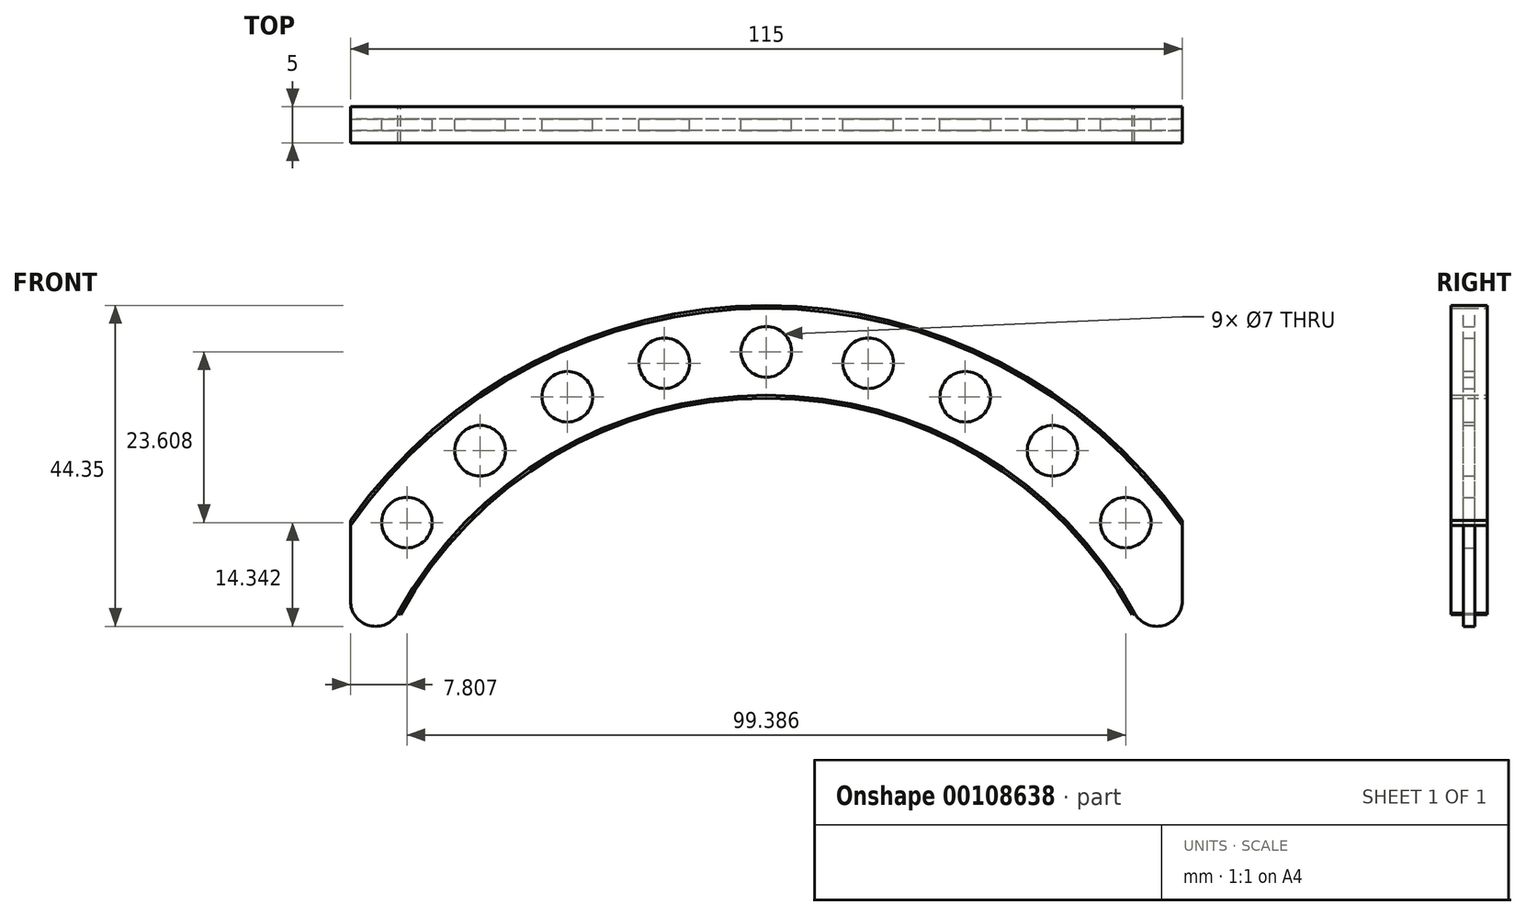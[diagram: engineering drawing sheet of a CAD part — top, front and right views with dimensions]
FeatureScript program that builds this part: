
annotation { "Feature Type Name" : "Feature", "Feature Type Description" : "" }
export const myFeature = defineFeature(function(context is Context, id is Id, definition is map)
    precondition{}
    {
        {
            var Q0;
            Q0=qCreatedBy(makeId("Front.planeOp"),FACE);
            var sketch = newSketch(context, id + "F0", { "sketchPlane" : qUnion([Q0])});
            skLineSegment(sketch, "E0", {"start": v(0, 0) * mm, "end": v(0, 92.04) * mm, "construction": true});
            skLineSegment(sketch, "E1", {"start": v(-57.5, 0) * mm, "end": v(-57.5, 0.7) * mm});
            skLineSegment(sketch, "E2", {"start": v(57.5, 0) * mm, "end": v(57.5, 0.7) * mm});
            skLineSegment(sketch, "E3", {"start": v(0, 0) * mm, "end": v(-57.5, 0) * mm});
            skLineSegment(sketch, "E4", {"start": v(0, 0) * mm, "end": v(57.5, 0) * mm});
            skLineSegment(sketch, "E5", {"start": v(17.72, 30) * mm, "end": v(-21.04, 30) * mm, "construction": true});
            skPoint(sketch, "E6", {"position": v(0, 30) * mm});
            skArc(sketch, "E7", {"start": v(57.5, 0) * mm, "mid": v(0, 30) * mm, "end": v(-57.5, 0) * mm});
            skArc(sketch, "E8.0", {"start": v(50.93, -12.14) * mm, "mid": v(0, 18) * mm, "end": v(-50.93, -12.14) * mm});
            skArc(sketch, "E9.0", {"start": v(52.58, -3.43) * mm, "mid": v(0, 24) * mm, "end": v(-52.58, -3.43) * mm});
            skLineSegment(sketch, "E10", {"start": v(57.5, 0) * mm, "end": v(57.5, -10.45) * mm});
            skLineSegment(sketch, "E11", {"start": v(-57.5, 0) * mm, "end": v(-57.5, -10.45) * mm});
            skCircle(sketch, "E12", {"center": v(0, 24) * mm, "radius": 3.5 * mm});
            skCircle(sketch, "E13.1.0", {"center": v(14.1, 22.43) * mm, "radius": 3.5 * mm});
            skCircle(sketch, "E13.2.0", {"center": v(27.5, 17.8) * mm, "radius": 3.5 * mm});
            skCircle(sketch, "E13.3.0", {"center": v(39.57, 10.33) * mm, "radius": 3.5 * mm});
            skCircle(sketch, "E13.4.0", {"center": v(49.7, 0.4) * mm, "radius": 3.5 * mm});
            skLineSegment(sketch, "E13.anchor1", {"start": v(0, -40.1) * mm, "end": v(0, 24) * mm, "construction": true});
            skLineSegment(sketch, "E13.anchor2", {"start": v(0, -40.1) * mm, "end": v(49.7, 0.4) * mm, "construction": true});
            skCircle(sketch, "E14.MirrorC", {"center": v(-49.7, 0.4) * mm, "radius": 3.5 * mm});
            skCircle(sketch, "E15.MirrorC", {"center": v(-39.57, 10.33) * mm, "radius": 3.5 * mm});
            skCircle(sketch, "E16.MirrorC", {"center": v(-27.5, 17.8) * mm, "radius": 3.5 * mm});
            skCircle(sketch, "E17.MirrorC", {"center": v(-14.1, 22.43) * mm, "radius": 3.5 * mm});
            skPoint(sketch, "E18.visualSharp", {"position": v(-57.5, -31.75) * mm});
            skArc(sketch, "E18.filletArc", {"start": v(-57.5, -10.45) * mm, "mid": v(-54.87, -13.85) * mm, "end": v(-50.93, -12.14) * mm});
            skPoint(sketch, "E19.visualSharp", {"position": v(57.5, -31.75) * mm});
            skArc(sketch, "E19.filletArc", {"start": v(50.93, -12.14) * mm, "mid": v(54.87, -13.85) * mm, "end": v(57.5, -10.45) * mm});
            skArc(sketch, "E20.0", {"start": v(57.5, 0.7) * mm, "mid": v(0, 30.4) * mm, "end": v(-57.5, 0.7) * mm});
            skLineSegment(sketch, "E21", {"start": v(57.5, 0.7) * mm, "end": v(57.5, 0) * mm});
            skArc(sketch, "E22.0", {"start": v(50.58, -12.33) * mm, "mid": v(0, 17.6) * mm, "end": v(-50.58, -12.33) * mm});
            skLineSegment(sketch, "E23", {"start": v(-50.93, -12.14) * mm, "end": v(-50.58, -12.33) * mm});
            skLineSegment(sketch, "E24", {"start": v(50.93, -12.14) * mm, "end": v(50.58, -12.33) * mm});
            skSolve(sketch);
        }
        {
            var Q0;
            {var subQ25=sQuery(id+"F0.wireOp",EDGE,"E7");Q0=makeQuery(id+"F0.imprint","IMPRINT",FACE,{"disambiguationData":[TD([[makeQuery(id+"F0.imprint","IMPRINT",EDGE,{"derivedFrom":subQ25}),1.0]])]});}
            var Q1;
            {var subQ18=sQuery(id+"F0.wireOp",EDGE,"E8.0");var subQ23=sQuery(id+"F0.wireOp",EDGE,"E3");var subQ24=makeQuery(id+"F0.imprint","INTERSECT",VERTEX,{"derivedFrom":[subQ23,subQ18]});Q1=makeQuery(id+"F0.imprint","IMPRINT",FACE,{"disambiguationData":[TD([[makeQuery(id+"F0.imprint","IMPRINT",EDGE,{"disambiguationData":[TD([[subQ24,-1.0]])],"derivedFrom":subQ23}),-1.0]])]});}
            var Q2;
            {var subQ0=sQuery(id+"F0.wireOp",EDGE,"E10");Q2=makeQuery(id+"F0.imprint","IMPRINT",FACE,{"disambiguationData":[TD([[makeQuery(id+"F0.imprint","IMPRINT",EDGE,{"derivedFrom":subQ0}),-1.0]])]});}
            var Q3;
            {var subQ4=sQuery(id+"F0.wireOp",EDGE,"E11");Q3=makeQuery(id+"F0.imprint","IMPRINT",FACE,{"disambiguationData":[TD([[makeQuery(id+"F0.imprint","IMPRINT",EDGE,{"derivedFrom":subQ4}),1.0]])]});}
            extrude(context, id + "F1", {"entities" : qUnion([Q0, Q1, Q2, Q3]), "endBound" : BoundingType.SYMMETRIC, "depth" : 1.6 * mm});
        }
        {
            var Q0;
            Q0=makeQuery(id+"F0.imprint","IMPRINT",FACE,{"disambiguationData":[TD([[makeQuery(id+"F0.imprint","IMPRINT",EDGE,{"derivedFrom":sQuery(id+"F0.wireOp",EDGE,"E7")}),-1.0]])]});
            extrude(context, id + "F2", {"entities" : qUnion([Q0]), "endBound" : BoundingType.SYMMETRIC, "depth" : 5 * mm});
        }
        {
            var Q0;
            {var subQ0=sQuery(id+"F0.wireOp",EDGE,"E22.0");var subQ1=sQuery(id+"F0.wireOp",EDGE,"E3");var subQ2=makeQuery(id+"F0.imprint","INTERSECT",VERTEX,{"derivedFrom":[subQ1,subQ0]});Q0=makeQuery(id+"F0.imprint","IMPRINT",FACE,{"disambiguationData":[TD([[makeQuery(id+"F0.imprint","IMPRINT",EDGE,{"disambiguationData":[TD([[subQ2,-1.0]])],"derivedFrom":subQ1}),-1.0]])]});}
            var Q1;
            {var subQ5=sQuery(id+"F0.wireOp",EDGE,"E24");Q1=makeQuery(id+"F0.imprint","IMPRINT",FACE,{"disambiguationData":[TD([[makeQuery(id+"F0.imprint","IMPRINT",EDGE,{"derivedFrom":subQ5}),-1.0]])]});}
            var Q2;
            {var subQ5=sQuery(id+"F0.wireOp",EDGE,"E23");Q2=makeQuery(id+"F0.imprint","IMPRINT",FACE,{"disambiguationData":[TD([[makeQuery(id+"F0.imprint","IMPRINT",EDGE,{"derivedFrom":subQ5}),1.0]])]});}
            extrude(context, id + "F3", {"entities" : qUnion([Q0, Q1, Q2]), "endBound" : BoundingType.SYMMETRIC, "depth" : 5 * mm});
        }
    });
